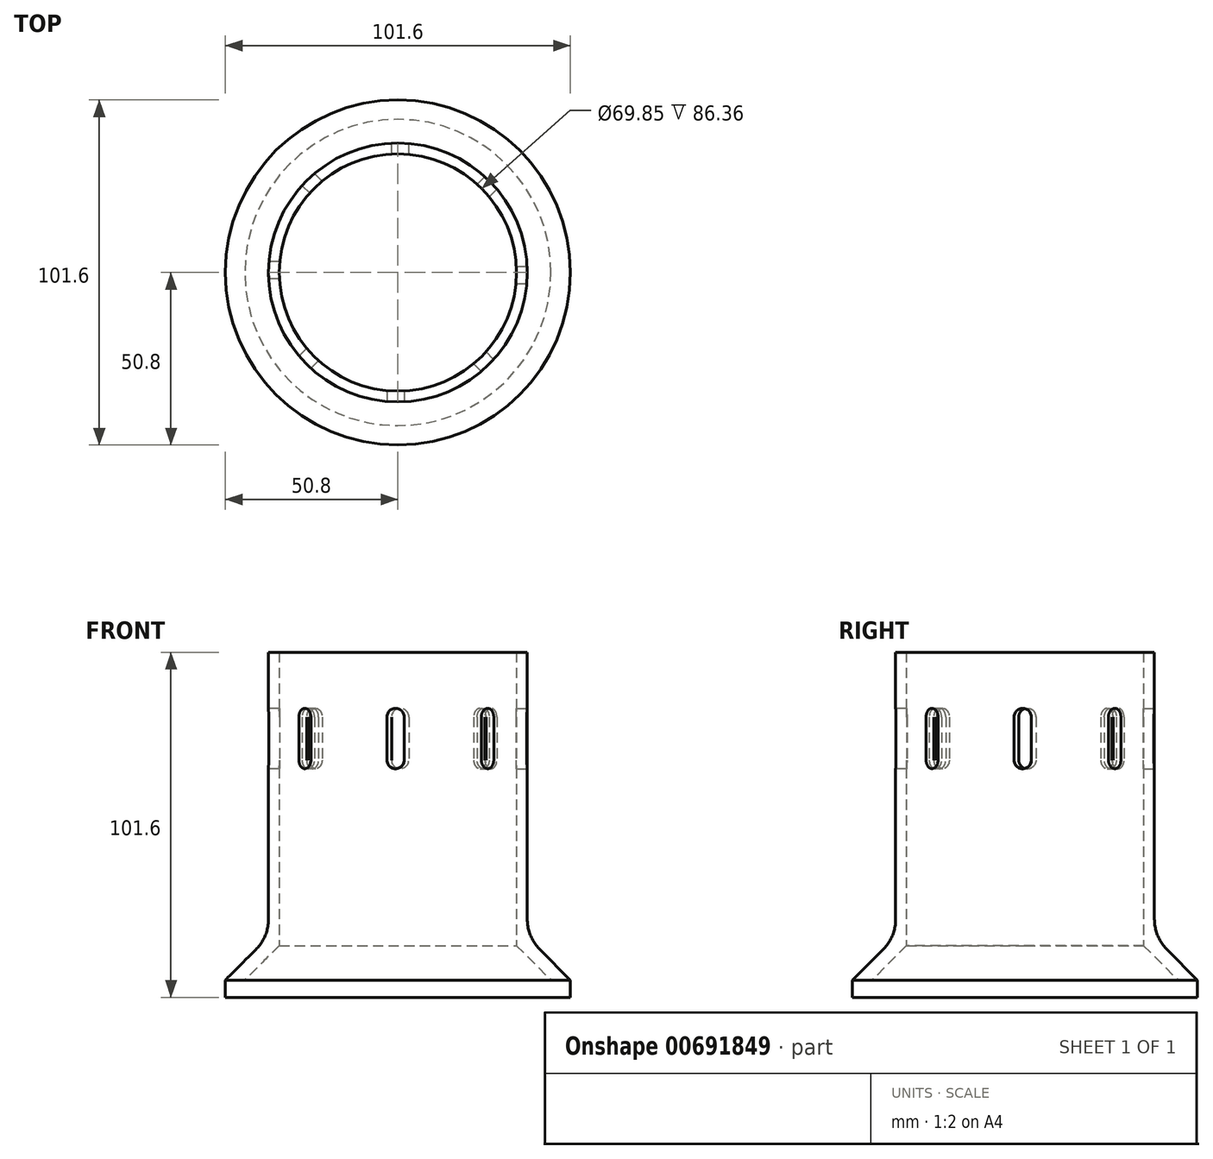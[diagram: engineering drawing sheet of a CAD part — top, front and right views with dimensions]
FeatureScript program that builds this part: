
annotation { "Feature Type Name" : "Feature", "Feature Type Description" : "" }
export const myFeature = defineFeature(function(context is Context, id is Id, definition is map)
    precondition{}
    {
        {
            var Q0;
            Q0=qCreatedBy(makeId("Front.planeOp"),FACE);
            var sketch = newSketch(context, id + "F0", { "sketchPlane" : qUnion([Q0])});
            skLineSegment(sketch, "E0", {"start": v(0, 5.08) * mm, "end": v(0, 101.6) * mm, "construction": true});
            skLineSegment(sketch, "E1", {"start": v(50.8, 0) * mm, "end": v(50.8, 5.08) * mm});
            skLineSegment(sketch, "E2", {"start": v(38.1, 63.33) * mm, "end": v(38.1, 17.78) * mm});
            skLineSegment(sketch, "E3", {"start": v(50.8, 5.08) * mm, "end": v(38.1, 17.78) * mm});
            skLineSegment(sketch, "E4", {"start": v(0, 0) * mm, "end": v(50.8, 0) * mm});
            skLineSegment(sketch, "E5", {"start": v(34.92, 63.33) * mm, "end": v(34.92, 15.24) * mm});
            skPoint(sketch, "E6.start.orphan", {"position": v(50.8, 2.54) * mm});
            skLineSegment(sketch, "E7", {"start": v(34.92, 101.6) * mm, "end": v(38.1, 101.6) * mm});
            skLineSegment(sketch, "E8", {"start": v(38.1, 63.33) * mm, "end": v(38.1, 101.6) * mm});
            skLineSegment(sketch, "E9", {"start": v(34.92, 63.33) * mm, "end": v(34.92, 101.6) * mm});
            skLineSegment(sketch, "E10", {"start": v(45.09, 5.08) * mm, "end": v(34.92, 15.24) * mm});
            skLineSegment(sketch, "E11", {"start": v(45.09, 5.08) * mm, "end": v(0, 5.08) * mm});
            skLineSegment(sketch, "E12", {"start": v(0, 0) * mm, "end": v(0, 5.08) * mm});
            skSolve(sketch);
        }
        {
            var Q0;
            Q0=makeQuery(id+"F0.imprint","IMPRINT",FACE,{"disambiguationData":[TD([[makeQuery(id+"F0.imprint","IMPRINT",EDGE,{"derivedFrom":sQuery(id+"F0.wireOp",EDGE,"E1")}),1.0]])]});
            var Q1;
            Q1=sQuery(id+"F0.wireOp",EDGE,"E0");
            revolve(context, id + "F1", {"entities" : qUnion([Q0]), "axis" : qUnion([Q1]), "revolveType" : RevolveType.FULL});
        }
        {
            var Q0;
            Q0=makeQuery(id+"F1.opRevolve","SWEPT_FACE",FACE,{"disambiguationData":[OSD([sQuery(id+"F0.wireOp",EDGE,"E7")])]});
            var sketch = newSketch(context, id + "F2", { "sketchPlane" : qUnion([Q0])});
            skLineSegment(sketch, "E13", {"start": v(0, 0) * mm, "end": v(0, -38.1) * mm, "construction": true});
            skSolve(sketch);
        }
        {
            var Q0;
            Q0=sQuery(id+"F2.wireOp",EDGE,"E13");
            var Q1;
            Q1=sQuery(id+"F2.wireOp",VERTEX,"E13.end");
            cPlane(context, id + "F3", {"entities" : qUnion([Q0, Q1]), "cplaneType" : CPlaneType.LINE_POINT, "offset" : 25.4 * mm, "width" : 152.4 * mm, "height" : 152.4 * mm});
        }
        {
            var Q0;
            Q0=qCreatedBy(id+"F3.planeOp",FACE);
            var sketch = newSketch(context, id + "F4", { "sketchPlane" : qUnion([Q0])});
            skLineSegment(sketch, "E14.trimOffspring", {"start": v(-0.68, 82.55) * mm, "end": v(0, 101.6) * mm, "construction": true});
            skArc(sketch, "E15", {"start": v(1.86, 82.55) * mm, "mid": v(-0.68, 85.1) * mm, "end": v(-3.22, 82.55) * mm});
            skLineSegment(sketch, "E16", {"start": v(-0.68, 82.55) * mm, "end": v(-0.68, 69.85) * mm, "construction": true});
            skArc(sketch, "E17", {"start": v(-3.22, 69.85) * mm, "mid": v(-0.68, 67.31) * mm, "end": v(1.86, 69.85) * mm});
            skLineSegment(sketch, "E18.0", {"start": v(-3.22, 82.55) * mm, "end": v(-3.22, 69.85) * mm});
            skLineSegment(sketch, "E19.0", {"start": v(1.86, 82.55) * mm, "end": v(1.86, 69.85) * mm});
            skSolve(sketch);
        }
        {
            var Q0;
            Q0=makeQuery(id+"F4.imprint","IMPRINT",FACE,{"disambiguationData":[TD([[makeQuery(id+"F4.imprint","IMPRINT",EDGE,{"derivedFrom":sQuery(id+"F4.wireOp",EDGE,"E15")}),1.0]])]});
            extrude(context, id + "F5", {"entities" : qUnion([Q0]), "operationType" : NewBodyOperationType.REMOVE, "oppositeDirection" : true, "depth" : 12.7 * mm, "offsetDistance" : 25.4 * mm});
        }
        {
            var Q0;
            Q0=makeQuery(id+"F5.boolean.opBoolean","COPY",FACE,{"derivedFrom":makeQuery(id+"F5.opExtrude","SWEPT_FACE",FACE,{"disambiguationData":[OSD([sQuery(id+"F4.wireOp",EDGE,"E19.0")])]})});
            var Q1;
            Q1=makeQuery(id+"F5.boolean.opBoolean","COPY",FACE,{"derivedFrom":makeQuery(id+"F5.opExtrude","SWEPT_FACE",FACE,{"disambiguationData":[OSD([sQuery(id+"F4.wireOp",EDGE,"E17")])]})});
            var Q2;
            Q2=makeQuery(id+"F5.boolean.opBoolean","COPY",FACE,{"derivedFrom":makeQuery(id+"F5.opExtrude","SWEPT_FACE",FACE,{"disambiguationData":[OSD([sQuery(id+"F4.wireOp",EDGE,"E18.0")])]})});
            var Q3;
            Q3=makeQuery(id+"F5.boolean.opBoolean","COPY",FACE,{"derivedFrom":makeQuery(id+"F5.opExtrude","SWEPT_FACE",FACE,{"disambiguationData":[OSD([sQuery(id+"F4.wireOp",EDGE,"E15")])]})});
            var Q4;
            Q4=makeQuery(id+"F1.opRevolve","SWEPT_EDGE",EDGE,{"disambiguationData":[OSD([sQuery(id+"F0.wireOp",EDGE,"E1"),sQuery(id+"F0.wireOp",EDGE,"E4")])]});
            circularPattern(context, id + "F6", {"patternType" : PatternType.FACE, "operationType" : NewBodyOperationType.REMOVE, "faces" : qUnion([Q0, Q1, Q2, Q3]), "axis" : qUnion([Q4]), "angle" : 360 * degree, "instanceCount" : 8, "equalSpace" : true});
        }
        {
            var Q0;
            Q0=makeQuery(id+"F1.opRevolve","SWEPT_EDGE",EDGE,{"disambiguationData":[OSD([sQuery(id+"F0.wireOp",EDGE,"E2"),sQuery(id+"F0.wireOp",EDGE,"E3")])]});
            fillet(context, id + "F7", {"entities" : qUnion([Q0]), "radius" : 12.7 * mm, "tangentPropagation" : true, "allowEdgeOverflow" : false});
        }
    });
